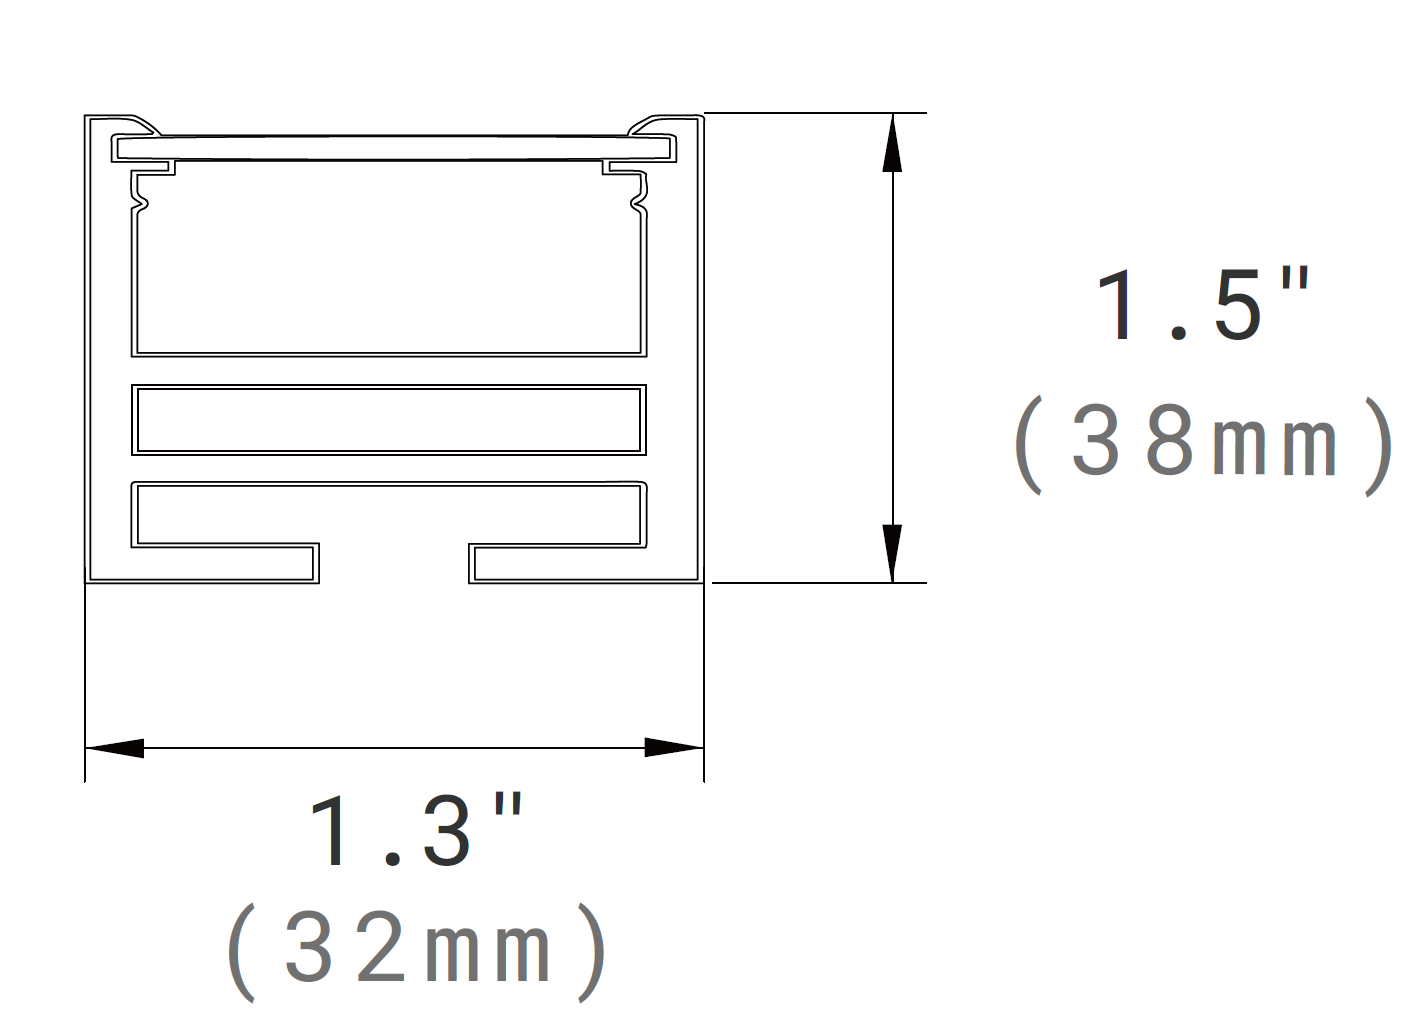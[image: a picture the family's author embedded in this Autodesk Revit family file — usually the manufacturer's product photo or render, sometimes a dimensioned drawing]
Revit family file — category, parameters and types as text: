
# Revit family: VRIO-DPMK
name_source: partatom
category: Lighting Fixtures
units: mm (PartAtom-declared; Revit-internal decimal feet)

## family parameters
Cut with Voids When Loaded = Yes
Host = Face
Light Source = Yes
Maintain Annotation Orientation = No
Part Type = Normal
Room Calculation Point = No
Round Connector Dimension = Use Diameter
Shared = No

## types (9) — shared parameters
Beam Angle = 0.00°
CRI = 90
Color Filter = 16777215
Default Elevation = 0' - 0"
Dimming Lamp Color Temperature Shift = <None>
Input Voltage = 120-277V
Lamp = LED
Load Classification = Lighting
Manufacturer = Above All Lighting
Power Factor = 0.9
Suspension = 3' - 0"
Tilt Angle = 90.00°

## per-type parameters (varying)
| type | 10'' Canopy 1 | 10'' Canopy 2 | 10'' Canopy 3 | 10'' Canopy 4 | 13.8'' Canopy | 200W 13.8'' Canopy | 300W 13.8'' Canopy | Cable Count | Canopy R | D1 | D1R | Model | Photometric Web File | R | Wattage Comments | cable |
| VRIO-65W-3000K-DPMK | Yes | No | No | No | No | No | No | 2 | 0' - 11 3/16" | 0' - 9 13/16" | 0' - 4 29/32" | VRIO-6524-30901-DPMK-WH | VRIO_6524_30901.ies | 0' - 11 13/16" | 65W | 0' - 11 25/32" |
| VRIO-80W-3000K-DPMK | No | Yes | No | No | No | No | No | 3 | 1' - 5 3/32" | 0' - 9 13/16" | 0' - 4 29/32" | VRD-5035-30901-ACPMK-WH | VRIO_8035_30901.ies | 1' - 5 11/16" | 80W | 1' - 5 21/32" |
| VRIO-120W-3000K-DPMK | No | Yes | No | No | No | No | No | 3 | 1' - 11" | 0' - 9 13/16" | 0' - 4 29/32" | VRIO-12047-30901-DPMK-WH | VRIO_12047_30901.ies | 1' - 11 19/32" | 120W | 1' - 11 9/16" |
| VRIO-135W-3000K-DPMK | No | Yes | No | No | No | No | No | 3 | 2' - 4 15/16" | 0' - 9 13/16" | 0' - 4 29/32" | VRIO-13559-30901-DPMK-WH | VRD_10059_30901.ies | 2' - 5 9/16" | 135W | 2' - 5 17/32" |
| VRIO-150W-3000K-DPMK | Yes | No | Yes | No | No | No | No | 4 | 3' - 2 13/16" | 0' - 9 13/16" | 0' - 4 29/32" | VRIO-15079-30901-DPMK-WH | generic | 3' - 3 13/32" | 150W | 3' - 3 3/8" |
| VRIO-200W-3000K-DPMK | Yes | No | No | No | No | Yes | No | 6 | 4' - 0 19/32" | 0' - 9 13/16" | 0' - 4 29/32" | VRIO-20098-30901-DPMK-WH | generic | 4' - 1 3/16" | 200W | 4' - 1 5/32" |
| VRIO-300W-3000K-DPMK | Yes | No | Yes | No | No | No | Yes | 7 | 4' - 10 7/16" | 0' - 9 13/16" | 0' - 4 29/32" | VRIO-300118-30901-DPMK-WH | generic | 4' - 11 1/16" | 300W | 4' - 11 1/32" |
| VRIO-400W-3000K-DPMK | Yes | Yes | Yes | No | No | No | No | 9 | 6' - 6 13/32" | 1' - 1 13/16" | 0' - 6 29/32" | VRIO-400158-30901-DPMK-WH | generic | 6' - 7" | 400W | 6' - 6 31/32" |
| VRIO-480W-3000K-DPMK | Yes | Yes | Yes | Yes | Yes | No | No | 12 | 7' - 8 1/4" | 0' - 9 13/16" | 0' - 4 29/32" | VRIO-480197-30901-DPMK-WH | generic | 7' - 8 27/32" | 480W | 7' - 8 13/16" |

## geometry (parser evidence)
native form markers: Sweep x2
no freeform markers — native parametric forms only
